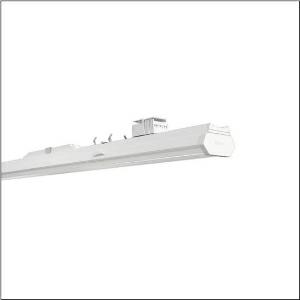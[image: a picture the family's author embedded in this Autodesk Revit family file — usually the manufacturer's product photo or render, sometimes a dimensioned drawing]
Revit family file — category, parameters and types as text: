
# Revit family: licross_r__21_performance_ho_52td16dn4e5m_0710
name_source: partatom
category: Lighting Fixtures
units: mm (PartAtom-declared; Revit-internal decimal feet)

## family parameters
Cut with Voids When Loaded = No
Host = Face
Light Source = No
Part Type = Normal
Room Calculation Point = No
Round Connector Dimension = Use Diameter
Shared = No

## types (1)
- --- (1 x LED, 14870 lm, 84.9 W, 4000K)
    Apparent Load = 85 VA
    CIE Flux Codes = 63 87 95 78 100
    Color Rendering = 80
    Color Temperature = 4000K
    Default Elevation = 1800 mm
    Description = Licross® 21 Performance HO, luminaire insert, of sheet steel, galvanised, coil coated, white, length: 1.500mm, width: 120mm, height: 123mm, LED rated luminous flux: 14.870lm, light colour: 840, control gear: DALI 2, control gear: ECG DALI, with plug, 5-pole, with phase selection, mains connection: 220..240V, AC, 50/60Hz, halogen-free wiring, primary light control with lens, of plastic, primary optical cover: cover, of PMMA, light emission: direct/indirect distribution, primary light characteristic: symmetric, protection rating (complete): IP54, insulation class (complete): insulation class I (protective earthing), certification: CE, ENEC, VDE, UKCA, protection symbol: D if used in an environment with non-conductive dust loads with corresponding accessories, impact resistance: IK06, permissible ambient temperature for indoor applications: -25..+35°C, corresponds to IFS (International Featured Standards) requirements for safety and quality in the food industry, reducing of maximum allowable ambient temperature of 5°C with ceiling mounting, LABS conformity tested according to VDMA 24364:2018-05, packaging unit: 1 piece
    Height = 114 mm
    Lamp = 1 x LED
    Lamp Light Flux = 14870 lm
    Lamp Power = 84.9 W
    Lamp count = 1
    Length = 1500 mm
    Luminous efficacy = 175 lm/W
    Manufacturer = Siteco
    ModVariant = No
    Model = 52TD16DN4E5M
    Mounting Place = Ceiling
    Mounting Type = Pendant
    Number of Poles = 1
    OnlyDefault = Yes
    Power Factor = 1
    Product Name = Licross® 21 Performance HO
    Product group = luminaire insert
    ProductGroupID = 902
    Protection Class = Protection class I
    Protection Degree = IP 54
    RLX_Detail_Level = 1
    RlxData = <blob elided: 31829 chars, md5=9538f525>
    Socket = socket
    Standby Power = 0 W
    System Light Flux = 14870 lm
    System Power = 85 W
    Type Comments = factory setting: luminous flux: 100 % | dim-lin: 254 | 484 mA
    Type Image = l_1256148.jpg
    URL = http://relux.com
    VarID = @adj_039627
    Voltage = 0 V
    Weight = 0.00 kg
    Width = 120 mm

## geometry (parser evidence)
native form markers: Blend x4, Sweep x11
no freeform markers — native parametric forms only
